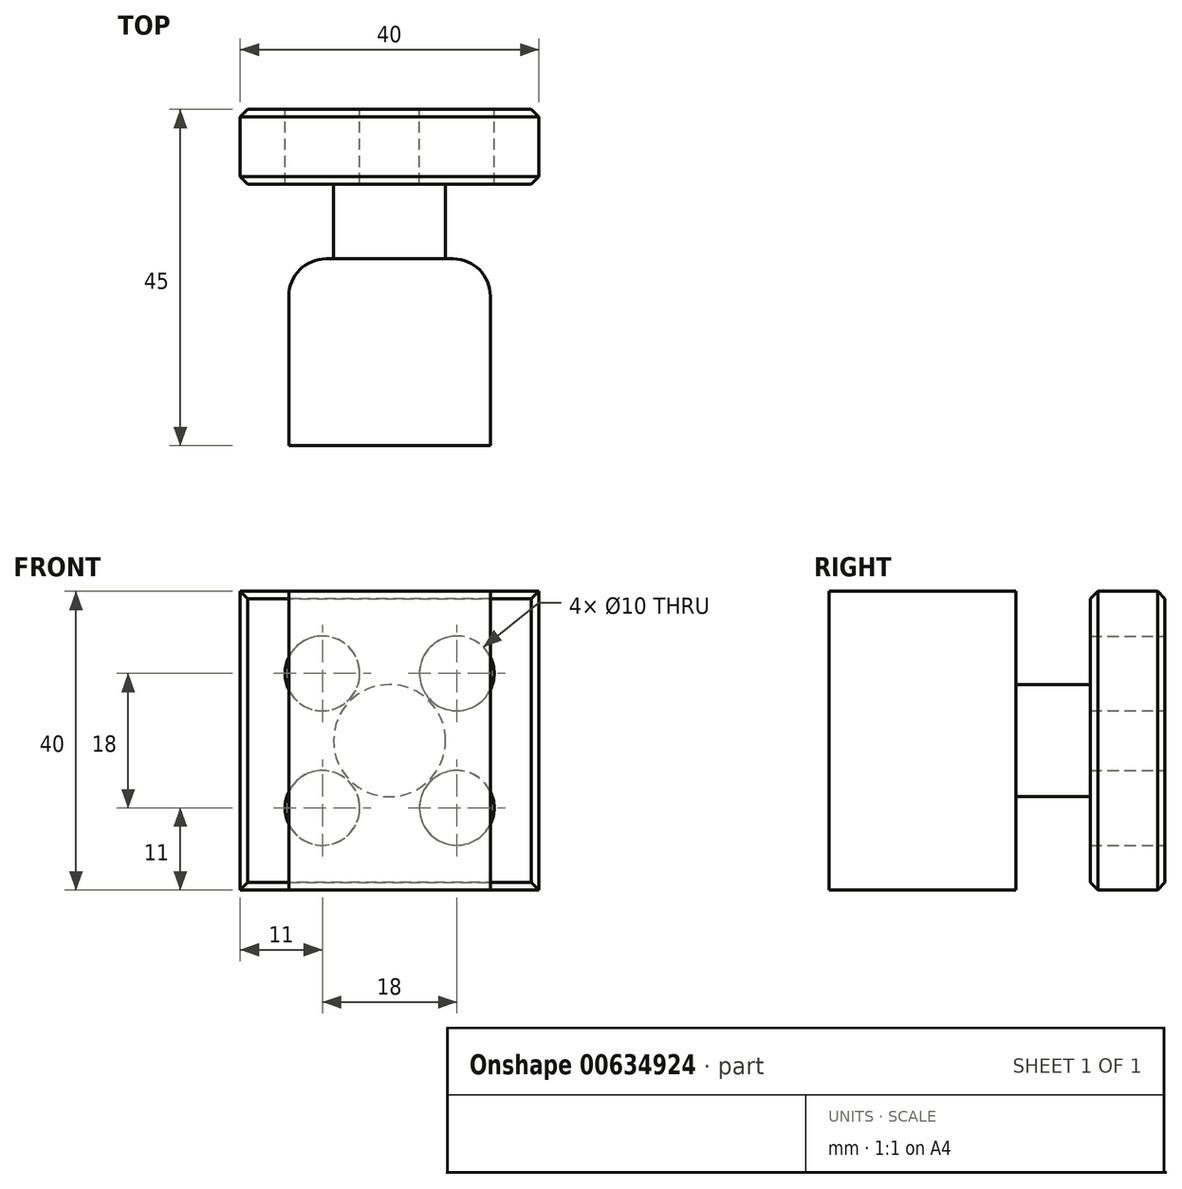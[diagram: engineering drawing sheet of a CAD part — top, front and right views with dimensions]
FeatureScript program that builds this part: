
annotation { "Feature Type Name" : "Feature", "Feature Type Description" : "" }
export const myFeature = defineFeature(function(context is Context, id is Id, definition is map)
    precondition{}
    {
        {
            var Q0;
            Q0=qCreatedBy(makeId("Top.planeOp"),FACE);
            var sketch = newSketch(context, id + "F0", { "sketchPlane" : qUnion([Q0])});
            skLineSegment(sketch, "E0.bottom", {"start": v(-13.5, 0) * mm, "end": v(13.5, 0) * mm});
            skLineSegment(sketch, "E0.top", {"start": v(-13.5, 25) * mm, "end": v(13.5, 25) * mm});
            skLineSegment(sketch, "E0.left", {"start": v(-13.5, 0) * mm, "end": v(-13.5, 25) * mm});
            skLineSegment(sketch, "E0.right", {"start": v(13.5, 0) * mm, "end": v(13.5, 25) * mm});
            skSolve(sketch);
        }
        {
            var Q0;
            Q0 = qSketchRegion(id + "F0", true);
            extrude(context, id + "F1", {"entities" : qUnion([Q0]), "depth" : 40 * mm, "offsetDistance" : 25 * mm});
        }
        {
            var Q0;
            Q0=makeQuery(id+"F1.opExtrude","SWEPT_EDGE",EDGE,{"disambiguationData":[OSD([sQuery(id+"F0.wireOp",EDGE,"E0.top"),sQuery(id+"F0.wireOp",EDGE,"E0.right")])]});
            var Q1;
            Q1=makeQuery(id+"F1.opExtrude","SWEPT_EDGE",EDGE,{"disambiguationData":[OSD([sQuery(id+"F0.wireOp",EDGE,"E0.top"),sQuery(id+"F0.wireOp",EDGE,"E0.left")])]});
            fillet(context, id + "F2", {"entities" : qUnion([Q0, Q1]), "radius" : 5 * mm, "tangentPropagation" : true, "allowEdgeOverflow" : false});
        }
        {
            var Q0;
            Q0=makeQuery(id+"F1.opExtrude","SWEPT_FACE",FACE,{"disambiguationData":[OSD([sQuery(id+"F0.wireOp",EDGE,"E0.top")])]});
            var sketch = newSketch(context, id + "F3", { "sketchPlane" : qUnion([Q0])});
            skCircle(sketch, "E1", {"center": v(0, 20) * mm, "radius": 7.5 * mm});
            skSolve(sketch);
        }
        {
            var Q0;
            Q0 = qSketchRegion(id + "F3", true);
            extrude(context, id + "F4", {"entities" : qUnion([Q0]), "operationType" : NewBodyOperationType.ADD, "depth" : 10 * mm, "offsetDistance" : 25 * mm});
        }
        {
            var Q0;
            Q0=makeQuery(id+"F4.opExtrude","CAP_FACE",FACE,{"disambiguationData":[OSD([sQuery(id+"F3.wireOp",EDGE,"E1")])],"isStart":false});
            var sketch = newSketch(context, id + "F5", { "sketchPlane" : qUnion([Q0])});
            skLineSegment(sketch, "E2.bottom", {"start": v(-20, 40) * mm, "end": v(20, 40) * mm});
            skLineSegment(sketch, "E2.top", {"start": v(-20, 0) * mm, "end": v(20, 0) * mm});
            skLineSegment(sketch, "E2.left", {"start": v(-20, 40) * mm, "end": v(-20, 0) * mm});
            skLineSegment(sketch, "E2.right", {"start": v(20, 40) * mm, "end": v(20, 0) * mm});
            skSolve(sketch);
        }
        {
            var Q0;
            Q0 = qSketchRegion(id + "F5", true);
            extrude(context, id + "F6", {"entities" : qUnion([Q0]), "operationType" : NewBodyOperationType.ADD, "depth" : 10 * mm, "offsetDistance" : 25 * mm});
        }
        {
            var Q0;
            Q0=makeQuery(id+"F6.opExtrude","CAP_EDGE",EDGE,{"disambiguationData":[OSD([sQuery(id+"F5.wireOp",EDGE,"E2.right")])],"isStart":false});
            var Q1;
            Q1=makeQuery(id+"F6.opExtrude","CAP_EDGE",EDGE,{"disambiguationData":[OSD([sQuery(id+"F5.wireOp",EDGE,"E2.bottom")])],"isStart":false});
            var Q2;
            Q2=makeQuery(id+"F6.opExtrude","CAP_EDGE",EDGE,{"disambiguationData":[OSD([sQuery(id+"F5.wireOp",EDGE,"E2.left")])],"isStart":false});
            var Q3;
            Q3=makeQuery(id+"F6.opExtrude","CAP_EDGE",EDGE,{"disambiguationData":[OSD([sQuery(id+"F5.wireOp",EDGE,"E2.top")])],"isStart":false});
            var Q4;
            Q4=makeQuery(id+"F6.opExtrude","CAP_EDGE",EDGE,{"disambiguationData":[OSD([sQuery(id+"F5.wireOp",EDGE,"E2.right")])],"isStart":true});
            var Q5;
            Q5=makeQuery(id+"F6.opExtrude","CAP_EDGE",EDGE,{"disambiguationData":[OSD([sQuery(id+"F5.wireOp",EDGE,"E2.bottom")])],"isStart":true});
            var Q6;
            Q6=makeQuery(id+"F6.opExtrude","CAP_EDGE",EDGE,{"disambiguationData":[OSD([sQuery(id+"F5.wireOp",EDGE,"E2.top")])],"isStart":true});
            var Q7;
            Q7=makeQuery(id+"F6.opExtrude","CAP_EDGE",EDGE,{"disambiguationData":[OSD([sQuery(id+"F5.wireOp",EDGE,"E2.left")])],"isStart":true});
            chamfer(context, id + "F7", {"entities" : qUnion([Q0, Q1, Q2, Q3, Q4, Q5, Q6, Q7]), "width" : 1 * mm, "tangentPropagation" : true});
        }
        {
            var Q0;
            Q0=makeQuery(id+"F6.opExtrude","CAP_FACE",FACE,{"disambiguationData":[OSD([sQuery(id+"F5.wireOp",EDGE,"E2.bottom"),sQuery(id+"F5.wireOp",EDGE,"E2.top"),sQuery(id+"F5.wireOp",EDGE,"E2.left"),sQuery(id+"F5.wireOp",EDGE,"E2.right")])],"isStart":false});
            var sketch = newSketch(context, id + "F8", { "sketchPlane" : qUnion([Q0])});
            skCircle(sketch, "E3", {"center": v(-9, 29) * mm, "radius": 5 * mm});
            skCircle(sketch, "E4", {"center": v(9, 29) * mm, "radius": 5 * mm});
            skCircle(sketch, "E5", {"center": v(-9, 11) * mm, "radius": 5 * mm});
            skCircle(sketch, "E6", {"center": v(9, 11) * mm, "radius": 5 * mm});
            skSolve(sketch);
        }
        {
            var Q0;
            Q0 = qSketchRegion(id + "F8", true);
            extrude(context, id + "F9", {"entities" : qUnion([Q0]), "operationType" : NewBodyOperationType.REMOVE, "oppositeDirection" : true, "depth" : 10 * mm, "offsetDistance" : 25 * mm});
        }
    });
